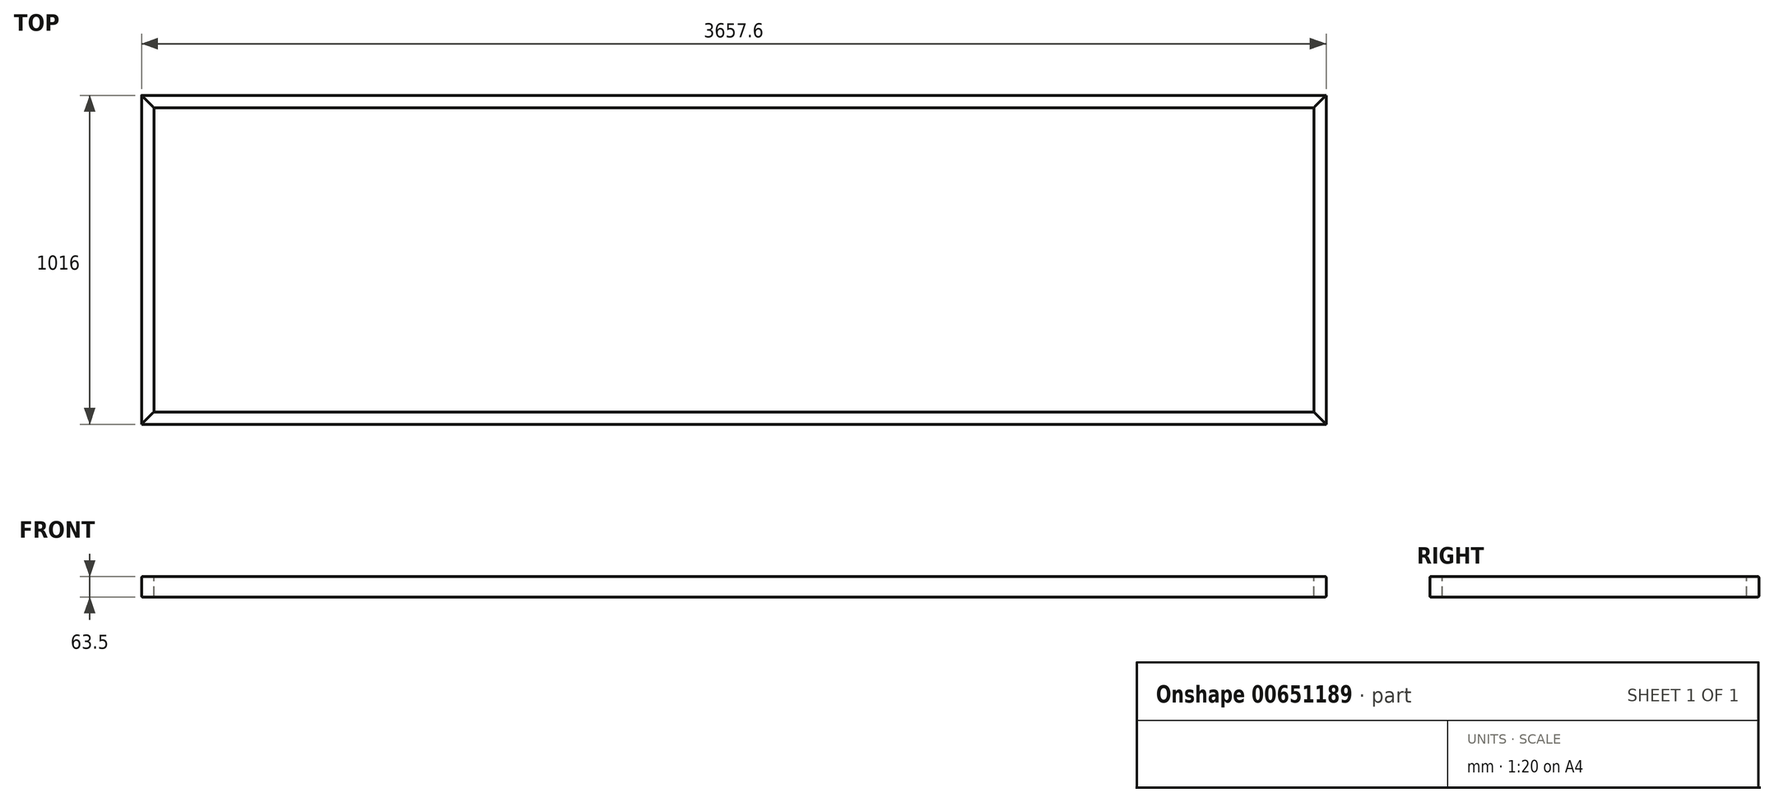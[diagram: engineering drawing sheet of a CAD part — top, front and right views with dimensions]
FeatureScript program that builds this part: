
annotation { "Feature Type Name" : "Feature", "Feature Type Description" : "" }
export const myFeature = defineFeature(function(context is Context, id is Id, definition is map)
    precondition{}
    {
        {
            var Q0;
            Q0=qCreatedBy(makeId("Top.planeOp"),FACE);
            var sketch = newSketch(context, id + "F0", { "sketchPlane" : qUnion([Q0])});
            skLineSegment(sketch, "E0", {"start": v(-1828.8, -508) * mm, "end": v(1828.8, -508) * mm});
            skLineSegment(sketch, "E1", {"start": v(1828.8, -508) * mm, "end": v(1790.7, -469.9) * mm});
            skLineSegment(sketch, "E2", {"start": v(1790.7, -469.9) * mm, "end": v(-1790.7, -469.9) * mm});
            skLineSegment(sketch, "E3", {"start": v(-1790.7, -469.9) * mm, "end": v(-1828.8, -508) * mm});
            skLineSegment(sketch, "E4", {"start": v(1828.8, -508) * mm, "end": v(1828.8, -466.51) * mm, "construction": true});
            skSolve(sketch);
        }
        {
            var Q0;
            Q0=makeQuery(id+"F0.imprint","IMPRINT",FACE,{"disambiguationData":[TD([[makeQuery(id+"F0.imprint","IMPRINT",EDGE,{"derivedFrom":sQuery(id+"F0.wireOp",EDGE,"E0")}),1.0]])]});
            extrude(context, id + "F1", {"entities" : qUnion([Q0]), "oppositeDirection" : true, "depth" : 63.5 * mm, "offsetDistance" : 25.4 * mm});
        }
        {
            var Q0;
            Q0=makeQuery(id+"F1.opExtrude","CAP_EDGE",EDGE,{"disambiguationData":[OSD([sQuery(id+"F0.wireOp",EDGE,"E0")])],"isStart":true});
            var Q1;
            Q1=makeQuery(id+"F1.opExtrude","CAP_EDGE",EDGE,{"disambiguationData":[OSD([sQuery(id+"F0.wireOp",EDGE,"E0")])],"isStart":false});
            var Q2;
            Q2=makeQuery(id+"F1.opExtrude","CAP_EDGE",EDGE,{"disambiguationData":[OSD([sQuery(id+"F0.wireOp",EDGE,"E2")])],"isStart":true});
            var Q3;
            Q3=makeQuery(id+"F1.opExtrude","CAP_EDGE",EDGE,{"disambiguationData":[OSD([sQuery(id+"F0.wireOp",EDGE,"E2")])],"isStart":false});
            fillet(context, id + "F2", {"entities" : qUnion([Q0, Q1, Q2, Q3]), "radius" : 3.17 * mm, "tangentPropagation" : true, "allowEdgeOverflow" : false});
        }
        {
            var Q0;
            Q0=qCreatedBy(makeId("Top.planeOp"),FACE);
            var sketch = newSketch(context, id + "F3", { "sketchPlane" : qUnion([Q0])});
            skLineSegment(sketch, "E5", {"start": v(-1790.7, 469.9) * mm, "end": v(-1828.8, 508) * mm});
            skLineSegment(sketch, "E6", {"start": v(-1828.8, 508) * mm, "end": v(1828.8, 508) * mm});
            skLineSegment(sketch, "E7", {"start": v(1828.8, 508) * mm, "end": v(1790.7, 469.9) * mm});
            skLineSegment(sketch, "E8", {"start": v(1790.7, 469.9) * mm, "end": v(-1790.7, 469.9) * mm});
            skLineSegment(sketch, "E9", {"start": v(1828.8, 508) * mm, "end": v(1828.8, 469.9) * mm, "construction": true});
            skSolve(sketch);
        }
        {
            var Q0;
            Q0=makeQuery(id+"F3.imprint","IMPRINT",FACE,{"disambiguationData":[TD([[makeQuery(id+"F3.imprint","IMPRINT",EDGE,{"derivedFrom":sQuery(id+"F3.wireOp",EDGE,"E5")}),-1.0]])]});
            extrude(context, id + "F4", {"entities" : qUnion([Q0]), "oppositeDirection" : true, "depth" : 63.5 * mm, "offsetDistance" : 25.4 * mm});
        }
        {
            var Q0;
            Q0=makeQuery(id+"F4.opExtrude","CAP_EDGE",EDGE,{"disambiguationData":[OSD([sQuery(id+"F3.wireOp",EDGE,"E8")])],"isStart":true});
            var Q1;
            Q1=makeQuery(id+"F4.opExtrude","CAP_EDGE",EDGE,{"disambiguationData":[OSD([sQuery(id+"F3.wireOp",EDGE,"E6")])],"isStart":true});
            var Q2;
            Q2=makeQuery(id+"F4.opExtrude","CAP_EDGE",EDGE,{"disambiguationData":[OSD([sQuery(id+"F3.wireOp",EDGE,"E8")])],"isStart":false});
            var Q3;
            Q3=makeQuery(id+"F4.opExtrude","CAP_EDGE",EDGE,{"disambiguationData":[OSD([sQuery(id+"F3.wireOp",EDGE,"E6")])],"isStart":false});
            fillet(context, id + "F5", {"entities" : qUnion([Q0, Q1, Q2, Q3]), "radius" : 3.17 * mm, "tangentPropagation" : true, "allowEdgeOverflow" : false});
        }
        {
            var Q0;
            Q0=qCreatedBy(makeId("Front.planeOp"),FACE);
            var sketch = newSketch(context, id + "F6", { "sketchPlane" : qUnion([Q0])});
            skLineSegment(sketch, "E10.0.0", {"start": v(1793.88, 0) * mm, "end": v(1825.63, 0) * mm});
            skArc(sketch, "E10.0.1", {"start": v(1825.63, 0) * mm, "mid": v(1827.87, -0.93) * mm, "end": v(1828.8, -3.17) * mm});
            skLineSegment(sketch, "E10.0.2", {"start": v(1828.8, -3.17) * mm, "end": v(1828.8, -60.33) * mm});
            skArc(sketch, "E10.0.3", {"start": v(1828.8, -60.33) * mm, "mid": v(1827.87, -62.57) * mm, "end": v(1825.63, -63.5) * mm});
            skLineSegment(sketch, "E10.0.4", {"start": v(1825.63, -63.5) * mm, "end": v(1793.88, -63.5) * mm});
            skArc(sketch, "E10.0.5", {"start": v(1793.88, -63.5) * mm, "mid": v(1791.63, -62.57) * mm, "end": v(1790.7, -60.33) * mm});
            skLineSegment(sketch, "E10.0.6", {"start": v(1790.7, -60.33) * mm, "end": v(1790.7, -3.17) * mm});
            skArc(sketch, "E10.0.7", {"start": v(1790.7, -3.17) * mm, "mid": v(1791.63, -0.93) * mm, "end": v(1793.88, 0) * mm});
            skSolve(sketch);
        }
        {
            var Q0;
            Q0=makeQuery(id+"F6.imprint","IMPRINT",FACE,{"disambiguationData":[TD([[makeQuery(id+"F6.imprint","IMPRINT",EDGE,{"derivedFrom":sQuery(id+"F6.wireOp",EDGE,"E10.0.0")}),-1.0]])]});
            extrude(context, id + "F7", {"entities" : qUnion([Q0]), "endBound" : BoundingType.UP_TO_NEXT, "depth" : 25.4 * mm, "offsetDistance" : 25.4 * mm, "hasSecondDirection" : true, "secondDirectionBound" : BoundingType.UP_TO_NEXT, "secondDirectionOppositeDirection" : true, "secondDirectionDepth" : 25.4 * mm});
        }
        {
            var Q0;
            Q0=qCreatedBy(makeId("Front.planeOp"),FACE);
            var sketch = newSketch(context, id + "F8", { "sketchPlane" : qUnion([Q0])});
            skLineSegment(sketch, "E11.0.0", {"start": v(-1828.8, -60.33) * mm, "end": v(-1828.8, -3.17) * mm});
            skArc(sketch, "E11.0.1", {"start": v(-1828.8, -3.17) * mm, "mid": v(-1827.87, -0.93) * mm, "end": v(-1825.63, 0) * mm});
            skLineSegment(sketch, "E11.0.2", {"start": v(-1825.63, 0) * mm, "end": v(-1793.88, 0) * mm});
            skArc(sketch, "E11.0.3", {"start": v(-1793.88, 0) * mm, "mid": v(-1791.63, -0.93) * mm, "end": v(-1790.7, -3.17) * mm});
            skLineSegment(sketch, "E11.0.4", {"start": v(-1790.7, -3.17) * mm, "end": v(-1790.7, -60.33) * mm});
            skArc(sketch, "E11.0.5", {"start": v(-1790.7, -60.33) * mm, "mid": v(-1791.63, -62.57) * mm, "end": v(-1793.88, -63.5) * mm});
            skLineSegment(sketch, "E11.0.6", {"start": v(-1793.88, -63.5) * mm, "end": v(-1825.63, -63.5) * mm});
            skArc(sketch, "E11.0.7", {"start": v(-1825.63, -63.5) * mm, "mid": v(-1827.87, -62.57) * mm, "end": v(-1828.8, -60.33) * mm});
            skSolve(sketch);
        }
        {
            var Q0;
            Q0=makeQuery(id+"F8.imprint","IMPRINT",FACE,{"disambiguationData":[TD([[makeQuery(id+"F8.imprint","IMPRINT",EDGE,{"derivedFrom":sQuery(id+"F8.wireOp",EDGE,"E11.0.0")}),-1.0]])]});
            extrude(context, id + "F9", {"entities" : qUnion([Q0]), "endBound" : BoundingType.UP_TO_NEXT, "depth" : 25.4 * mm, "offsetDistance" : 25.4 * mm, "hasSecondDirection" : true, "secondDirectionBound" : BoundingType.UP_TO_NEXT, "secondDirectionOppositeDirection" : true, "secondDirectionDepth" : 25.4 * mm});
        }
    });
